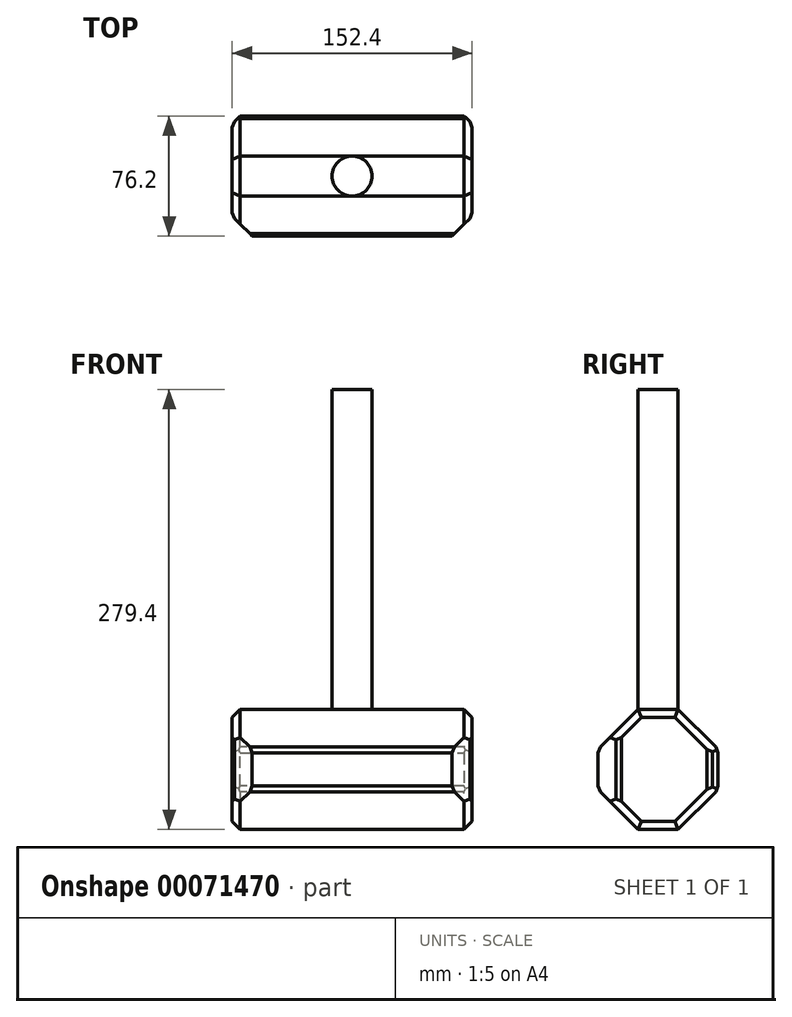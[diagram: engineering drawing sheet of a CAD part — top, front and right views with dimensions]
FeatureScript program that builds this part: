
annotation { "Feature Type Name" : "Feature", "Feature Type Description" : "" }
export const myFeature = defineFeature(function(context is Context, id is Id, definition is map)
    precondition{}
    {
        {
            var Q0;
            Q0=qCreatedBy(makeId("Top.planeOp"),FACE);
            var sketch = newSketch(context, id + "F0", { "sketchPlane" : qUnion([Q0])});
            skLineSegment(sketch, "E0.rect.bottom", {"start": v(76.2, 38.1) * mm, "end": v(-76.2, 38.1) * mm});
            skLineSegment(sketch, "E0.rect.top", {"start": v(76.2, -38.1) * mm, "end": v(-76.2, -38.1) * mm});
            skLineSegment(sketch, "E0.rect.left", {"start": v(76.2, 38.1) * mm, "end": v(76.2, -38.1) * mm});
            skLineSegment(sketch, "E0.rect.right", {"start": v(-76.2, 38.1) * mm, "end": v(-76.2, -38.1) * mm});
            skPoint(sketch, "E0.rect.middle", {"position": v(0, 0) * mm});
            skSolve(sketch);
        }
        {
            var Q0;
            Q0=makeQuery(id+"F0.imprint","IMPRINT",FACE,{"disambiguationData":[TD([[makeQuery(id+"F0.imprint","IMPRINT",EDGE,{"derivedFrom":sQuery(id+"F0.wireOp",EDGE,"E0.rect.bottom")}),1.0]])]});
            extrude(context, id + "F1", {"entities" : qUnion([Q0]), "depth" : 76.2 * mm});
        }
        {
            var Q0;
            Q0=makeQuery(id+"F1.opExtrude","CAP_EDGE",EDGE,{"disambiguationData":[OSD([sQuery(id+"F0.wireOp",EDGE,"E0.rect.bottom")])],"isStart":true});
            chamfer(context, id + "F2", {"entities" : qUnion([Q0]), "width" : 25.4 * mm, "tangentPropagation" : true});
        }
        {
            var Q0;
            Q0=makeQuery(id+"F1.opExtrude","CAP_EDGE",EDGE,{"disambiguationData":[OSD([sQuery(id+"F0.wireOp",EDGE,"E0.rect.bottom")])],"isStart":false});
            var Q1;
            Q1=makeQuery(id+"F1.opExtrude","CAP_EDGE",EDGE,{"disambiguationData":[OSD([sQuery(id+"F0.wireOp",EDGE,"E0.rect.top")])],"isStart":true});
            chamfer(context, id + "F3", {"entities" : qUnion([Q0, Q1]), "width" : 25.4 * mm, "tangentPropagation" : true});
        }
        {
            var Q0;
            {var subQ0=sQuery(id+"F0.wireOp",EDGE,"E0.rect.bottom");Q0=makeQuery(id+"F3.opChamfer","BLEND_EDGE",EDGE,{"blendedFrom":[makeQuery(id+"F1.opExtrude","CAP_EDGE",EDGE,{"disambiguationData":[OSD([subQ0])],"isStart":false}),makeQuery(id+"F1.opExtrude","SWEPT_FACE",FACE,{"disambiguationData":[OSD([subQ0])]})],"blendedInto":[makeQuery(id+"F1.opExtrude","SWEPT_FACE",FACE,{"disambiguationData":[OSD([subQ0])]})]});}
            var Q1;
            {var subQ0=sQuery(id+"F0.wireOp",EDGE,"E0.rect.bottom");Q1=makeQuery(id+"F2.opChamfer","BLEND_EDGE",EDGE,{"blendedFrom":[makeQuery(id+"F1.opExtrude","CAP_EDGE",EDGE,{"disambiguationData":[OSD([subQ0])],"isStart":true}),makeQuery(id+"F1.opExtrude","SWEPT_FACE",FACE,{"disambiguationData":[OSD([subQ0])]})],"blendedInto":[makeQuery(id+"F1.opExtrude","SWEPT_FACE",FACE,{"disambiguationData":[OSD([subQ0])]})]});}
            var Q2;
            Q2=makeQuery(id+"F1.opExtrude","SWEPT_EDGE",EDGE,{"disambiguationData":[OSD([sQuery(id+"F0.wireOp",EDGE,"E0.rect.bottom"),sQuery(id+"F0.wireOp",EDGE,"E0.rect.right")])]});
            var Q3;
            Q3=makeQuery(id+"F1.opExtrude","SWEPT_EDGE",EDGE,{"disambiguationData":[OSD([sQuery(id+"F0.wireOp",EDGE,"E0.rect.bottom"),sQuery(id+"F0.wireOp",EDGE,"E0.rect.left")])]});
            chamfer(context, id + "F4", {"entities" : qUnion([Q0, Q1, Q2, Q3]), "width" : 5.08 * mm, "tangentPropagation" : true});
        }
        {
            var Q0;
            Q0=makeQuery(id+"F1.opExtrude","SWEPT_EDGE",EDGE,{"disambiguationData":[OSD([sQuery(id+"F0.wireOp",EDGE,"E0.rect.top"),sQuery(id+"F0.wireOp",EDGE,"E0.rect.left")])]});
            var Q1;
            {var subQ0=sQuery(id+"F0.wireOp",EDGE,"E0.rect.top");Q1=makeQuery(id+"FEoKxJFafaepJN1_1.opChamfer","BLEND_EDGE",EDGE,{"blendedFrom":[makeQuery(id+"F1.opExtrude","SWEPT_EDGE",EDGE,{"disambiguationData":[OSD([subQ0,sQuery(id+"F0.wireOp",EDGE,"E0.rect.right")])]}),makeQuery(id+"F1.opExtrude","SWEPT_FACE",FACE,{"disambiguationData":[OSD([subQ0])]})],"blendedInto":[makeQuery(id+"F1.opExtrude","SWEPT_FACE",FACE,{"disambiguationData":[OSD([subQ0])]})]});}
            chamfer(context, id + "F5", {"entities" : qUnion([Q0, Q1]), "width" : 12.7 * mm, "tangentPropagation" : true});
        }
        {
            var Q0;
            {var subQ0=sQuery(id+"F0.wireOp",EDGE,"E0.rect.top");Q0=makeQuery(id+"FEoKxJFafaepJN1_1.opChamfer","BLEND_EDGE",EDGE,{"blendedFrom":[makeQuery(id+"F1.opExtrude","CAP_EDGE",EDGE,{"disambiguationData":[OSD([subQ0])],"isStart":false}),makeQuery(id+"F1.opExtrude","SWEPT_FACE",FACE,{"disambiguationData":[OSD([subQ0])]})],"blendedInto":[makeQuery(id+"F1.opExtrude","SWEPT_FACE",FACE,{"disambiguationData":[OSD([subQ0])]})]});}
            var Q1;
            {var subQ0=sQuery(id+"F0.wireOp",EDGE,"E0.rect.top");Q1=makeQuery(id+"F3.opChamfer","BLEND_EDGE",EDGE,{"blendedFrom":[makeQuery(id+"F1.opExtrude","CAP_EDGE",EDGE,{"disambiguationData":[OSD([subQ0])],"isStart":true}),makeQuery(id+"F1.opExtrude","SWEPT_FACE",FACE,{"disambiguationData":[OSD([subQ0])]})],"blendedInto":[makeQuery(id+"F1.opExtrude","SWEPT_FACE",FACE,{"disambiguationData":[OSD([subQ0])]})]});}
            chamfer(context, id + "F6", {"entities" : qUnion([Q0, Q1]), "width" : 5.08 * mm, "tangentPropagation" : true});
        }
        {
            var Q0;
            Q0=makeQuery(id+"F1.opExtrude","CAP_EDGE",EDGE,{"disambiguationData":[OSD([sQuery(id+"F0.wireOp",EDGE,"E0.rect.top")])],"isStart":false});
            chamfer(context, id + "F7", {"entities" : qUnion([Q0]), "width" : 25.4 * mm, "tangentPropagation" : true});
        }
        {
            var Q0;
            {var subQ0=sQuery(id+"F0.wireOp",EDGE,"E0.rect.top");Q0=makeQuery(id+"F7.opChamfer","BLEND_EDGE",EDGE,{"blendedFrom":[makeQuery(id+"F1.opExtrude","CAP_EDGE",EDGE,{"disambiguationData":[OSD([subQ0])],"isStart":false}),makeQuery(id+"F1.opExtrude","SWEPT_FACE",FACE,{"disambiguationData":[OSD([subQ0])]})],"blendedInto":[makeQuery(id+"F1.opExtrude","SWEPT_FACE",FACE,{"disambiguationData":[OSD([subQ0])]})]});}
            chamfer(context, id + "F8", {"entities" : qUnion([Q0]), "width" : 5.08 * mm, "tangentPropagation" : true});
        }
        {
            var Q0;
            Q0=makeQuery(id+"F1.opExtrude","SWEPT_EDGE",EDGE,{"disambiguationData":[OSD([sQuery(id+"F0.wireOp",EDGE,"E0.rect.top"),sQuery(id+"F0.wireOp",EDGE,"E0.rect.right")])]});
            chamfer(context, id + "F9", {"entities" : qUnion([Q0]), "width" : 12.7 * mm, "tangentPropagation" : true});
        }
        {
            var Q0;
            Q0=makeQuery(id+"F1.opExtrude","CAP_EDGE",EDGE,{"disambiguationData":[OSD([sQuery(id+"F0.wireOp",EDGE,"E0.rect.right")])],"isStart":false});
            var Q1;
            Q1=makeQuery(id+"F1.opExtrude","SWEPT_FACE",FACE,{"disambiguationData":[OSD([sQuery(id+"F0.wireOp",EDGE,"E0.rect.right")])]});
            chamfer(context, id + "F10", {"entities" : qUnion([Q0, Q1]), "width" : 5.08 * mm, "tangentPropagation" : true});
        }
        {
            var Q0;
            Q0=makeQuery(id+"F1.opExtrude","SWEPT_FACE",FACE,{"disambiguationData":[OSD([sQuery(id+"F0.wireOp",EDGE,"E0.rect.left")])]});
            chamfer(context, id + "F11", {"entities" : qUnion([Q0]), "width" : 5.08 * mm, "tangentPropagation" : true});
        }
        {
            var Q0;
            Q0=makeQuery(id+"F1.opExtrude","CAP_FACE",FACE,{"disambiguationData":[OSD([sQuery(id+"F0.wireOp",EDGE,"E0.rect.bottom"),sQuery(id+"F0.wireOp",EDGE,"E0.rect.top"),sQuery(id+"F0.wireOp",EDGE,"E0.rect.left"),sQuery(id+"F0.wireOp",EDGE,"E0.rect.right")])],"isStart":false});
            var sketch = newSketch(context, id + "F12", { "sketchPlane" : qUnion([Q0])});
            skCircle(sketch, "E1", {"center": v(0, 0) * mm, "radius": 12.7 * mm});
            skSolve(sketch);
        }
        {
            var Q0;
            Q0 = qSketchRegion(id + "F12", true);
            extrude(context, id + "F13", {"entities" : qUnion([Q0]), "operationType" : NewBodyOperationType.ADD, "depth" : 203.2 * mm});
        }
    });
